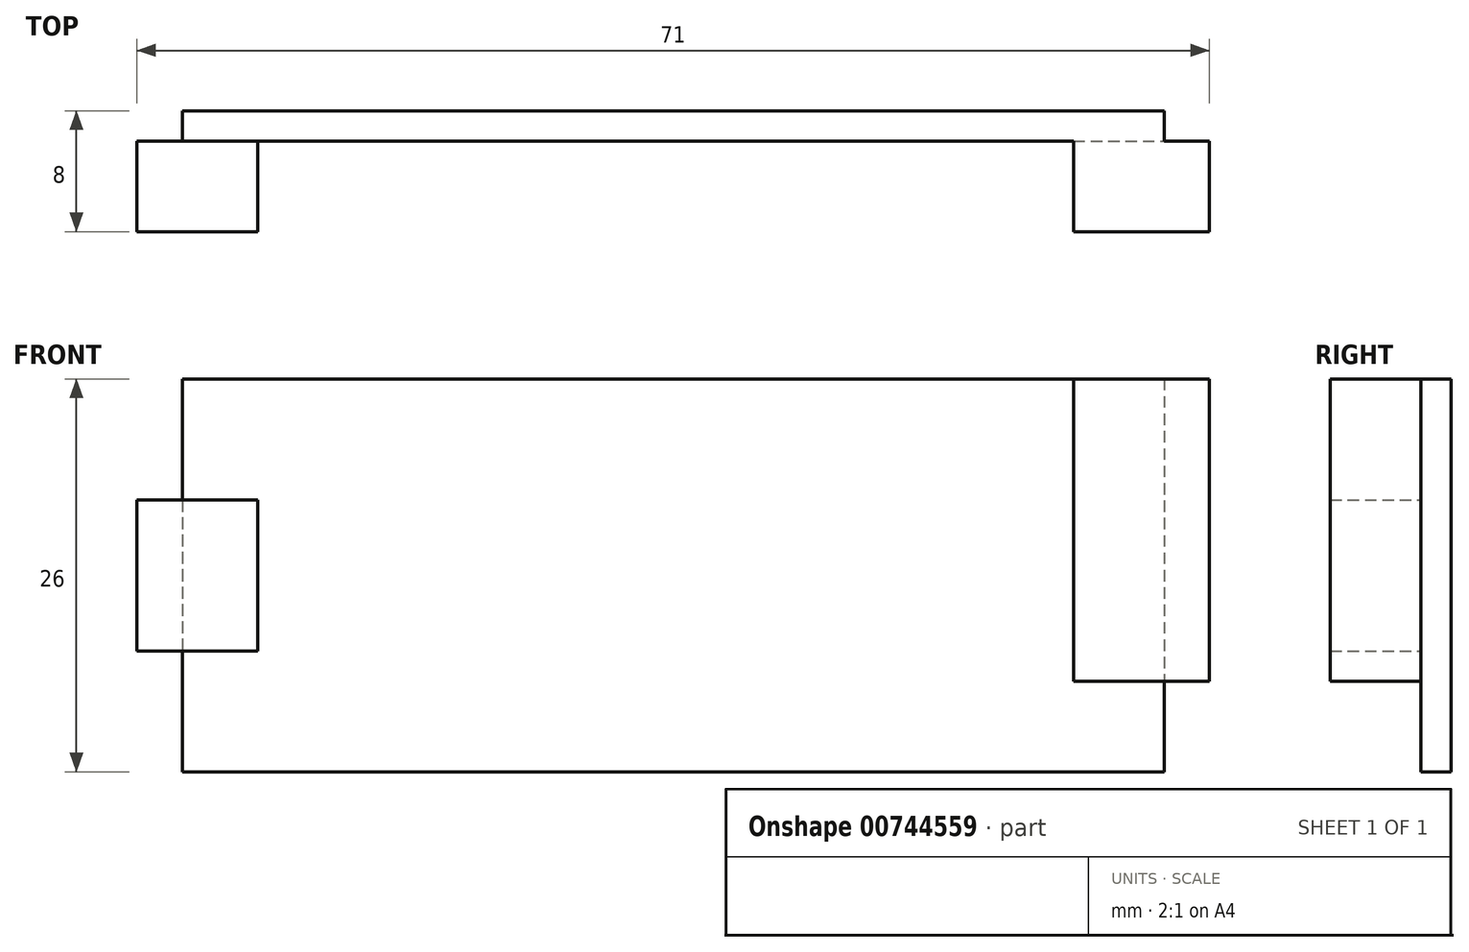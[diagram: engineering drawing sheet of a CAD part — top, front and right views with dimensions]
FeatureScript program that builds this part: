
annotation { "Feature Type Name" : "Feature", "Feature Type Description" : "" }
export const myFeature = defineFeature(function(context is Context, id is Id, definition is map)
    precondition{}
    {
        {
            var Q0;
            Q0=qCreatedBy(makeId("Front.planeOp"),FACE);
            var sketch = newSketch(context, id + "F0", { "sketchPlane" : qUnion([Q0])});
            skLineSegment(sketch, "E0.bottom", {"start": v(-32.5, 13) * mm, "end": v(32.5, 13) * mm});
            skLineSegment(sketch, "E0.top", {"start": v(-32.5, -13) * mm, "end": v(32.5, -13) * mm});
            skLineSegment(sketch, "E0.left", {"start": v(-32.5, 13) * mm, "end": v(-32.5, -13) * mm});
            skLineSegment(sketch, "E0.right", {"start": v(32.5, 13) * mm, "end": v(32.5, -13) * mm});
            skSolve(sketch);
        }
        {
            var Q0;
            Q0 = qSketchRegion(id + "F0", true);
            extrude(context, id + "F1", {"entities" : qUnion([Q0]), "depth" : 2 * mm, "offsetDistance" : 25 * mm});
        }
        {
            var Q0;
            Q0=makeQuery(id+"F1.opExtrude","CAP_FACE",FACE,{"disambiguationData":[OSD([sQuery(id+"F0.wireOp",EDGE,"E0.bottom"),sQuery(id+"F0.wireOp",EDGE,"E0.top"),sQuery(id+"F0.wireOp",EDGE,"E0.left"),sQuery(id+"F0.wireOp",EDGE,"E0.right")])],"isStart":false});
            var sketch = newSketch(context, id + "F2", { "sketchPlane" : qUnion([Q0])});
            skLineSegment(sketch, "E1.bottom", {"start": v(-27.5, 5) * mm, "end": v(-35.5, 5) * mm});
            skLineSegment(sketch, "E1.top", {"start": v(-27.5, -5) * mm, "end": v(-35.5, -5) * mm});
            skLineSegment(sketch, "E1.left", {"start": v(-27.5, 5) * mm, "end": v(-27.5, -5) * mm});
            skLineSegment(sketch, "E1.right", {"start": v(-35.5, 5) * mm, "end": v(-35.5, -5) * mm});
            skLineSegment(sketch, "E2.bottom", {"start": v(26.5, 13) * mm, "end": v(35.5, 13) * mm});
            skLineSegment(sketch, "E2.top", {"start": v(26.5, -7) * mm, "end": v(35.5, -7) * mm});
            skLineSegment(sketch, "E2.left", {"start": v(26.5, 13) * mm, "end": v(26.5, -7) * mm});
            skLineSegment(sketch, "E2.right", {"start": v(35.5, 13) * mm, "end": v(35.5, -7) * mm});
            skSolve(sketch);
        }
        {
            var Q0;
            {var subQ0=sQuery(id+"F2.wireOp",EDGE,"E1.right");Q0=makeQuery(id+"F2.imprint","IMPRINT",FACE,{"disambiguationData":[TD([[makeQuery(id+"F2.imprint","IMPRINT",EDGE,{"derivedFrom":subQ0}),1.0]])]});}
            var Q1;
            {var subQ0=sQuery(id+"F2.wireOp",EDGE,"E1.left");Q1=makeQuery(id+"F2.imprint","IMPRINT",FACE,{"disambiguationData":[TD([[makeQuery(id+"F2.imprint","IMPRINT",EDGE,{"derivedFrom":subQ0}),-1.0]])]});}
            var Q2;
            {var subQ3=sQuery(id+"F2.wireOp",EDGE,"E2.left");Q2=makeQuery(id+"F2.imprint","IMPRINT",FACE,{"disambiguationData":[TD([[makeQuery(id+"F2.imprint","IMPRINT",EDGE,{"derivedFrom":subQ3}),1.0]])]});}
            var Q3;
            {var subQ3=sQuery(id+"F2.wireOp",EDGE,"E2.right");Q3=makeQuery(id+"F2.imprint","IMPRINT",FACE,{"disambiguationData":[TD([[makeQuery(id+"F2.imprint","IMPRINT",EDGE,{"derivedFrom":subQ3}),-1.0]])]});}
            extrude(context, id + "F3", {"entities" : qUnion([Q0, Q1, Q2, Q3]), "operationType" : NewBodyOperationType.ADD, "depth" : 6 * mm, "offsetDistance" : 25 * mm});
        }
    });
